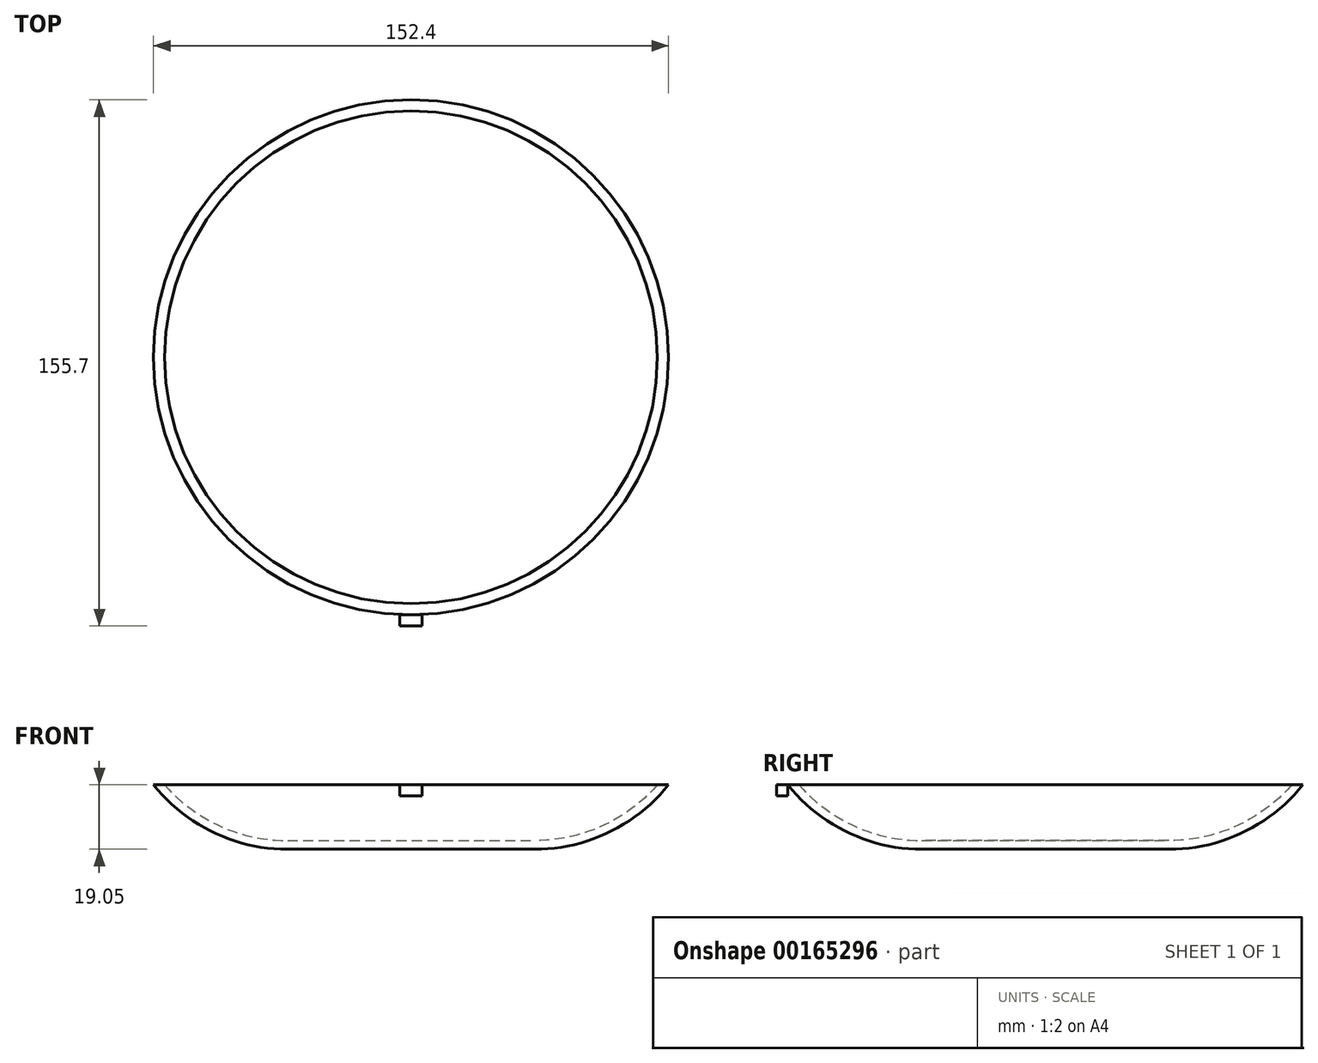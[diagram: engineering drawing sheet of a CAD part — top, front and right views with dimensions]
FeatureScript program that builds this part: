
annotation { "Feature Type Name" : "Feature", "Feature Type Description" : "" }
export const myFeature = defineFeature(function(context is Context, id is Id, definition is map)
    precondition{}
    {
        {
            var Q0;
            Q0=qCreatedBy(makeId("Top.planeOp"),FACE);
            var sketch = newSketch(context, id + "F0", { "sketchPlane" : qUnion([Q0])});
            skCircle(sketch, "E0", {"center": v(0, 0) * mm, "radius": 76.2 * mm});
            skSolve(sketch);
        }
        {
            var Q0;
            Q0=makeQuery(id+"F0.imprint","IMPRINT",FACE,{"disambiguationData":[TD([[makeQuery(id+"F0.imprint","IMPRINT",EDGE,{"derivedFrom":sQuery(id+"F0.wireOp",EDGE,"E0")}),1.0]])]});
            extrude(context, id + "F1", {"entities" : qUnion([Q0]), "depth" : 19.05 * mm});
        }
        {
            var Q0;
            Q0=makeQuery(id+"F1.opExtrude","CAP_FACE",FACE,{"disambiguationData":[OSD([sQuery(id+"F0.wireOp",EDGE,"E0")])],"isStart":true});
            fillet(context, id + "F2", {"entities" : qUnion([Q0]), "radius" : 50.8 * mm, "tangentPropagation" : true, "allowEdgeOverflow" : false});
        }
        {
            var Q0;
            Q0=makeQuery(id+"F1.opExtrude","CAP_FACE",FACE,{"disambiguationData":[OSD([sQuery(id+"F0.wireOp",EDGE,"J5YnjgUa-Xol7-oKWa-l3Hr-sc4Rq7JUCeJf")])],"isStart":false});
            var Q1;
            Q1=makeQuery(id+"F1.opExtrude","CAP_FACE",FACE,{"disambiguationData":[OSD([sQuery(id+"F0.wireOp",EDGE,"E0")])],"isStart":false});
            shell(context, id + "F3", {"entities" : qUnion([Q0, Q1]), "thickness" : 2.54 * mm});
        }
        {
            var Q0;
            Q0=makeQuery(id+"F1.opExtrude","CAP_FACE",FACE,{"disambiguationData":[OSD([sQuery(id+"F0.wireOp",EDGE,"E0")])],"isStart":false});
            var sketch = newSketch(context, id + "F4", { "sketchPlane" : qUnion([Q0])});
            skLineSegment(sketch, "E1", {"start": v(0, -76.2) * mm, "end": v(-3.3, -76.2) * mm});
            skLineSegment(sketch, "E2", {"start": v(0, -76.2) * mm, "end": v(3.3, -76.2) * mm});
            skLineSegment(sketch, "E3", {"start": v(-3.3, -76.2) * mm, "end": v(-3.3, -79.5) * mm});
            skLineSegment(sketch, "E4", {"start": v(3.3, -76.2) * mm, "end": v(3.3, -79.5) * mm});
            skLineSegment(sketch, "E5", {"start": v(3.3, -79.5) * mm, "end": v(-3.3, -79.5) * mm});
            skSolve(sketch);
        }
        {
            var Q0;
            Q0=makeQuery(id+"F4.imprint","IMPRINT",FACE,{"disambiguationData":[TD([[makeQuery(id+"F4.imprint","IMPRINT",EDGE,{"derivedFrom":sQuery(id+"F4.wireOp",EDGE,"E1")}),1.0]])]});
            extrude(context, id + "F5", {"entities" : qUnion([Q0]), "oppositeDirection" : true, "depth" : 3.3 * mm});
        }
    });
